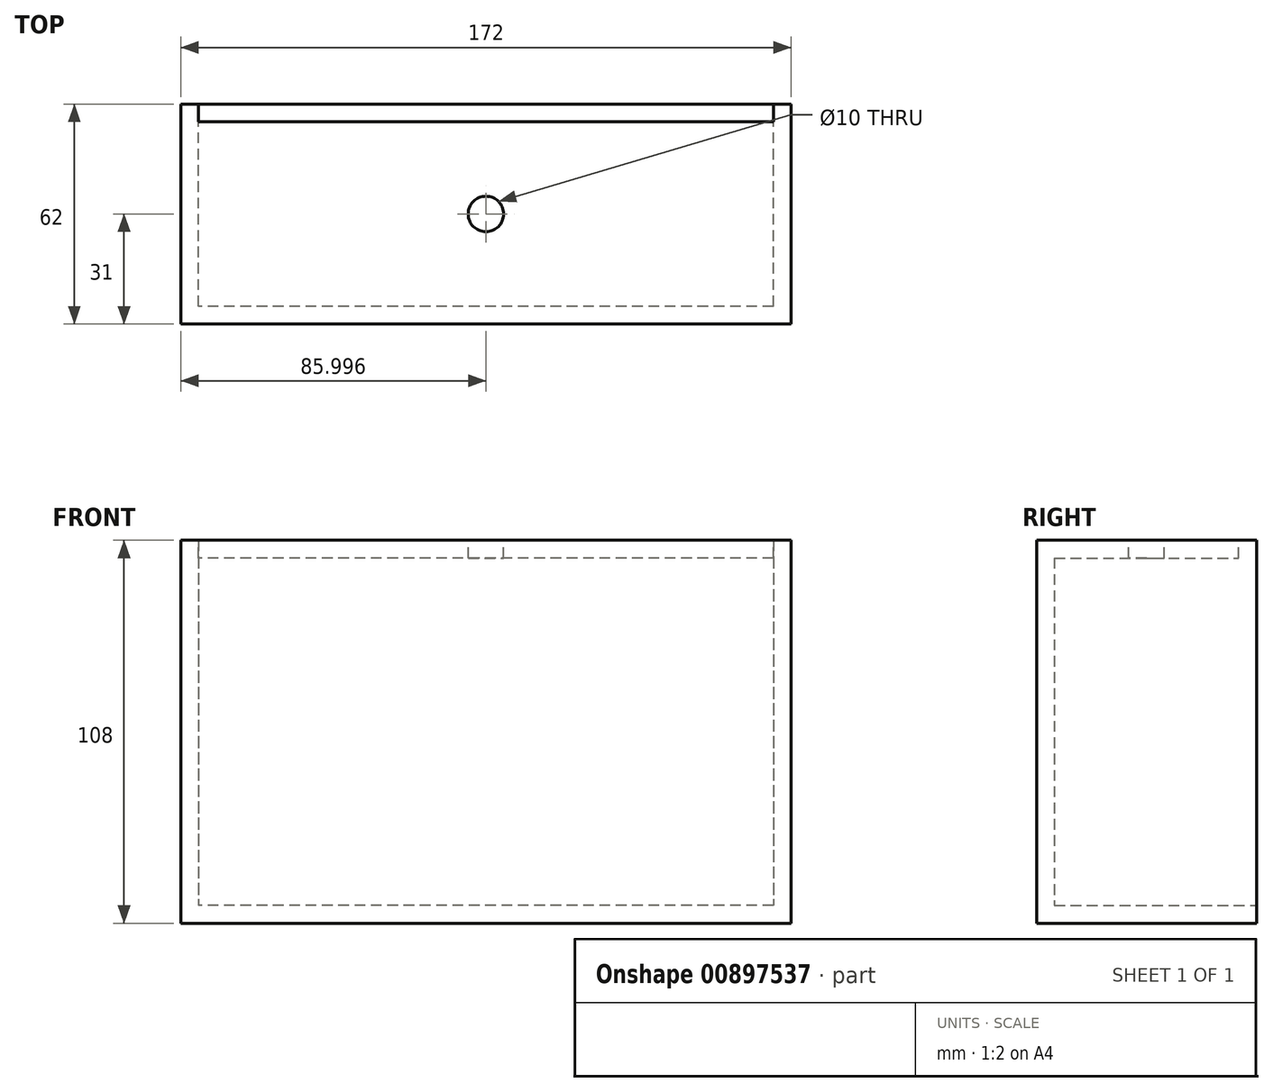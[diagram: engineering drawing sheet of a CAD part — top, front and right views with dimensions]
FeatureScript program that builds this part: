
annotation { "Feature Type Name" : "Feature", "Feature Type Description" : "" }
export const myFeature = defineFeature(function(context is Context, id is Id, definition is map)
    precondition{}
    {
        {
            var Q0;
            Q0=qCreatedBy(makeId("Front.planeOp"),FACE);
            var sketch = newSketch(context, id + "F0", { "sketchPlane" : qUnion([Q0])});
            skLineSegment(sketch, "E0.bottom", {"start": v(-79.58, 54.39) * mm, "end": v(92.42, 54.39) * mm});
            skLineSegment(sketch, "E0.top", {"start": v(-79.58, -53.61) * mm, "end": v(92.42, -53.61) * mm});
            skLineSegment(sketch, "E0.left", {"start": v(-79.58, 54.39) * mm, "end": v(-79.58, -53.61) * mm});
            skLineSegment(sketch, "E0.right", {"start": v(92.42, 54.39) * mm, "end": v(92.42, -53.61) * mm});
            skSolve(sketch);
        }
        {
            var Q0;
            Q0=makeQuery(id+"F0.imprint","IMPRINT",FACE,{"disambiguationData":[TD([[makeQuery(id+"F0.imprint","IMPRINT",EDGE,{"derivedFrom":sQuery(id+"F0.wireOp",EDGE,"E0.bottom")}),-1.0]])]});
            extrude(context, id + "F1", {"entities" : qUnion([Q0]), "depth" : 62 * mm, "offsetDistance" : 25 * mm});
        }
        {
            var Q0;
            Q0=makeQuery(id+"F1.opExtrude","SWEPT_FACE",FACE,{"disambiguationData":[OSD([sQuery(id+"F0.wireOp",EDGE,"E0.bottom")])]});
            var sketch = newSketch(context, id + "F2", { "sketchPlane" : qUnion([Q0])});
            skCircle(sketch, "E1", {"center": v(6.42, -31) * mm, "radius": 5 * mm});
            skSolve(sketch);
        }
        {
            var Q0;
            Q0=makeQuery(id+"F1.opExtrude","CAP_FACE",FACE,{"disambiguationData":[OSD([sQuery(id+"F0.wireOp",EDGE,"E0.bottom"),sQuery(id+"F0.wireOp",EDGE,"E0.top"),sQuery(id+"F0.wireOp",EDGE,"E0.left"),sQuery(id+"F0.wireOp",EDGE,"E0.right")])],"isStart":true});
            var sketch = newSketch(context, id + "F3", { "sketchPlane" : qUnion([Q0])});
            skLineSegment(sketch, "E2.bottom", {"start": v(-87.42, 49.39) * mm, "end": v(74.58, 49.39) * mm});
            skLineSegment(sketch, "E2.top", {"start": v(-87.42, -48.61) * mm, "end": v(74.58, -48.61) * mm});
            skLineSegment(sketch, "E2.left", {"start": v(-87.42, 49.39) * mm, "end": v(-87.42, -48.61) * mm});
            skLineSegment(sketch, "E2.right", {"start": v(74.58, 49.39) * mm, "end": v(74.58, -48.61) * mm});
            skSolve(sketch);
        }
        {
            var Q0;
            Q0=makeQuery(id+"F3.imprint","IMPRINT",FACE,{"disambiguationData":[TD([[makeQuery(id+"F3.imprint","IMPRINT",EDGE,{"derivedFrom":sQuery(id+"F3.wireOp",EDGE,"E2.bottom")}),-1.0]])]});
            extrude(context, id + "F4", {"entities" : qUnion([Q0]), "operationType" : NewBodyOperationType.REMOVE, "oppositeDirection" : true, "depth" : 57 * mm, "offsetDistance" : 25 * mm});
        }
        {
            var Q0;
            Q0=makeQuery(id+"F2.imprint","IMPRINT",FACE,{"disambiguationData":[TD([[makeQuery(id+"F2.imprint","IMPRINT",EDGE,{"derivedFrom":sQuery(id+"F2.wireOp",EDGE,"E1")}),1.0]])]});
            extrude(context, id + "F5", {"entities" : qUnion([Q0]), "operationType" : NewBodyOperationType.REMOVE, "oppositeDirection" : true, "depth" : 25 * mm, "offsetDistance" : 25 * mm});
        }
        {
            var Q0;
            Q0=makeQuery(id+"F1.opExtrude","SWEPT_FACE",FACE,{"disambiguationData":[OSD([sQuery(id+"F0.wireOp",EDGE,"E0.bottom")])]});
            var sketch = newSketch(context, id + "F6", { "sketchPlane" : qUnion([Q0])});
            skLineSegment(sketch, "E3.bottom", {"start": v(-74.58, 0) * mm, "end": v(87.42, 0) * mm});
            skLineSegment(sketch, "E3.top", {"start": v(-74.58, -5) * mm, "end": v(87.42, -5) * mm});
            skLineSegment(sketch, "E3.left", {"start": v(-74.58, 0) * mm, "end": v(-74.58, -5) * mm});
            skLineSegment(sketch, "E3.right", {"start": v(87.42, 0) * mm, "end": v(87.42, -5) * mm});
            skSolve(sketch);
        }
        {
            var Q0;
            Q0=makeQuery(id+"F6.imprint","IMPRINT",FACE,{"disambiguationData":[TD([[makeQuery(id+"F6.imprint","IMPRINT",EDGE,{"derivedFrom":sQuery(id+"F6.wireOp",EDGE,"E3.bottom")}),-1.0]])]});
            extrude(context, id + "F7", {"entities" : qUnion([Q0]), "operationType" : NewBodyOperationType.REMOVE, "oppositeDirection" : true, "depth" : 25 * mm, "offsetDistance" : 25 * mm});
        }
    });
